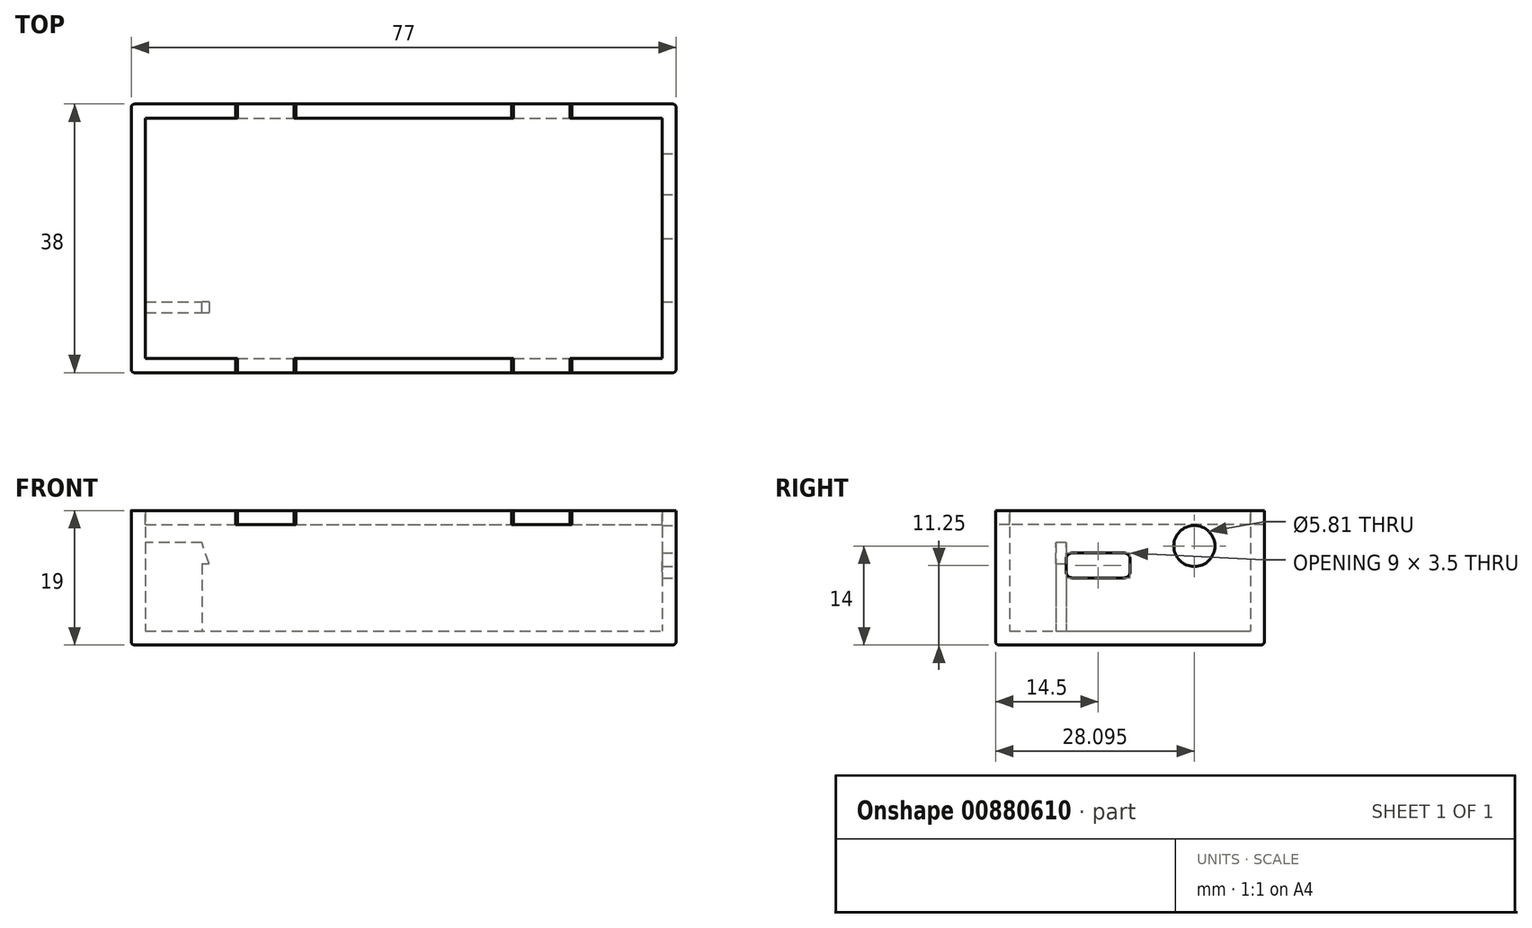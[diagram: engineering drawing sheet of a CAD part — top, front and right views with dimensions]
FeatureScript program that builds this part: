
annotation { "Feature Type Name" : "Feature", "Feature Type Description" : "" }
export const myFeature = defineFeature(function(context is Context, id is Id, definition is map)
    precondition{}
    {
        {
            var Q0;
            Q0=qCreatedBy(makeId("Top.planeOp"),FACE);
            var sketch = newSketch(context, id + "F0", { "sketchPlane" : qUnion([Q0])});
            skLineSegment(sketch, "E0.bottom", {"start": v(0, 0) * mm, "end": v(73, 0) * mm});
            skLineSegment(sketch, "E0.top", {"start": v(0, 34) * mm, "end": v(73, 34) * mm});
            skLineSegment(sketch, "E0.left", {"start": v(0, 0) * mm, "end": v(0, 34) * mm});
            skLineSegment(sketch, "E0.right", {"start": v(73, 0) * mm, "end": v(73, 34) * mm});
            skSolve(sketch);
        }
        {
            var Q0;
            Q0=makeQuery(id+"F0.imprint","IMPRINT",FACE,{"disambiguationData":[TD([[makeQuery(id+"F0.imprint","IMPRINT",EDGE,{"derivedFrom":sQuery(id+"F0.wireOp",EDGE,"E0.bottom")}),1.0]])]});
            extrude(context, id + "F1", {"entities" : qUnion([Q0]), "depth" : 17 * mm, "offsetDistance" : 25.4 * mm});
        }
        {
            var Q0;
            Q0=makeQuery(id+"F1.opExtrude","CAP_FACE",FACE,{"disambiguationData":[OSD([sQuery(id+"F0.wireOp",EDGE,"E0.bottom"),sQuery(id+"F0.wireOp",EDGE,"E0.top"),sQuery(id+"F0.wireOp",EDGE,"E0.left"),sQuery(id+"F0.wireOp",EDGE,"E0.right")])],"isStart":false});
            shell(context, id + "F2", {"entities" : qUnion([Q0]), "thickness" : 2 * mm, "oppositeDirection" : true});
        }
        {
            var Q0;
            Q0=makeQuery(id+"F1.opExtrude","SWEPT_FACE",FACE,{"disambiguationData":[OSD([sQuery(id+"F0.wireOp",EDGE,"E0.right")])]});
            var sketch = newSketch(context, id + "F3", { "sketchPlane" : qUnion([Q0])});
            skLineSegment(sketch, "E1.bottom", {"start": v(8, 11) * mm, "end": v(17, 11) * mm});
            skLineSegment(sketch, "E1.top", {"start": v(8, 7.5) * mm, "end": v(17, 7.5) * mm});
            skLineSegment(sketch, "E1.left", {"start": v(8, 11) * mm, "end": v(8, 7.5) * mm});
            skLineSegment(sketch, "E1.right", {"start": v(17, 11) * mm, "end": v(17, 7.5) * mm});
            skSolve(sketch);
        }
        {
            var Q0;
            Q0 = qSketchRegion(id + "F3", true);
            extrude(context, id + "F4", {"entities" : qUnion([Q0]), "operationType" : NewBodyOperationType.REMOVE, "oppositeDirection" : true, "depth" : 25.4 * mm, "offsetDistance" : 25.4 * mm});
        }
        {
            var Q0;
            Q0=makeQuery(id+"F1.opExtrude","SWEPT_FACE",FACE,{"disambiguationData":[OSD([sQuery(id+"F0.wireOp",EDGE,"E0.right")])]});
            var sketch = newSketch(context, id + "F5", { "sketchPlane" : qUnion([Q0])});
            skLineSegment(sketch, "E2", {"start": v(17.2, 12) * mm, "end": v(26.1, 12) * mm, "construction": true});
            skCircle(sketch, "E3", {"center": v(26.1, 12) * mm, "radius": 2.9 * mm});
            skSolve(sketch);
        }
        {
            var Q0;
            Q0 = qSketchRegion(id + "F5", true);
            extrude(context, id + "F6", {"entities" : qUnion([Q0]), "operationType" : NewBodyOperationType.REMOVE, "oppositeDirection" : true, "depth" : 25.4 * mm, "offsetDistance" : 25.4 * mm});
        }
        {
            var Q0;
            Q0=makeQuery(id+"F4.boolean.opBoolean","COPY",EDGE,{"derivedFrom":makeQuery(id+"F4.opExtrude","SWEPT_EDGE",EDGE,{"disambiguationData":[OSD([sQuery(id+"F3.wireOp",EDGE,"E1.top"),sQuery(id+"F3.wireOp",EDGE,"E1.left")])]})});
            var Q1;
            Q1=makeQuery(id+"F4.boolean.opBoolean","COPY",EDGE,{"derivedFrom":makeQuery(id+"F4.opExtrude","SWEPT_EDGE",EDGE,{"disambiguationData":[OSD([sQuery(id+"F3.wireOp",EDGE,"E1.bottom"),sQuery(id+"F3.wireOp",EDGE,"E1.right")])]})});
            var Q2;
            Q2=makeQuery(id+"F4.boolean.opBoolean","COPY",EDGE,{"derivedFrom":makeQuery(id+"F4.opExtrude","SWEPT_EDGE",EDGE,{"disambiguationData":[OSD([sQuery(id+"F3.wireOp",EDGE,"E1.top"),sQuery(id+"F3.wireOp",EDGE,"E1.right")])]})});
            var Q3;
            Q3=makeQuery(id+"F4.boolean.opBoolean","COPY",EDGE,{"derivedFrom":makeQuery(id+"F4.opExtrude","SWEPT_EDGE",EDGE,{"disambiguationData":[OSD([sQuery(id+"F3.wireOp",EDGE,"E1.bottom"),sQuery(id+"F3.wireOp",EDGE,"E1.left")])]})});
            fillet(context, id + "F7", {"entities" : qUnion([Q0, Q1, Q2, Q3]), "radius" : .8 * mm, "tangentPropagation" : true, "allowEdgeOverflow" : false});
        }
        {
            var Q0;
            Q0=makeQuery(id+"F1.opExtrude","SWEPT_EDGE",EDGE,{"disambiguationData":[OSD([sQuery(id+"F0.wireOp",EDGE,"E0.top"),sQuery(id+"F0.wireOp",EDGE,"E0.right")])]});
            var Q1;
            Q1=makeQuery(id+"F1.opExtrude","SWEPT_EDGE",EDGE,{"disambiguationData":[OSD([sQuery(id+"F0.wireOp",EDGE,"E0.top"),sQuery(id+"F0.wireOp",EDGE,"E0.left")])]});
            var Q2;
            Q2=makeQuery(id+"F1.opExtrude","SWEPT_EDGE",EDGE,{"disambiguationData":[OSD([sQuery(id+"F0.wireOp",EDGE,"E0.bottom"),sQuery(id+"F0.wireOp",EDGE,"E0.left")])]});
            var Q3;
            Q3=makeQuery(id+"F1.opExtrude","SWEPT_EDGE",EDGE,{"disambiguationData":[OSD([sQuery(id+"F0.wireOp",EDGE,"E0.bottom"),sQuery(id+"F0.wireOp",EDGE,"E0.right")])]});
            var Q4;
            Q4=makeQuery(id+"F1.opExtrude","CAP_EDGE",EDGE,{"disambiguationData":[OSD([sQuery(id+"F0.wireOp",EDGE,"E0.top")])],"isStart":true});
            var Q5;
            Q5=makeQuery(id+"F1.opExtrude","CAP_EDGE",EDGE,{"disambiguationData":[OSD([sQuery(id+"F0.wireOp",EDGE,"E0.right")])],"isStart":true});
            var Q6;
            Q6=makeQuery(id+"F1.opExtrude","CAP_EDGE",EDGE,{"disambiguationData":[OSD([sQuery(id+"F0.wireOp",EDGE,"E0.bottom")])],"isStart":true});
            var Q7;
            Q7=makeQuery(id+"F1.opExtrude","CAP_EDGE",EDGE,{"disambiguationData":[OSD([sQuery(id+"F0.wireOp",EDGE,"E0.left")])],"isStart":true});
            fillet(context, id + "F8", {"entities" : qUnion([Q0, Q1, Q2, Q3, Q4, Q5, Q6, Q7]), "radius" : .5 * mm, "tangentPropagation" : true, "allowEdgeOverflow" : false});
        }
        {
            var Q0;
            Q0=makeQuery(id+"F1.opExtrude","CAP_FACE",FACE,{"disambiguationData":[OSD([sQuery(id+"F0.wireOp",EDGE,"E0.bottom"),sQuery(id+"F0.wireOp",EDGE,"E0.top"),sQuery(id+"F0.wireOp",EDGE,"E0.left"),sQuery(id+"F0.wireOp",EDGE,"E0.right")])],"isStart":false});
            var sketch = newSketch(context, id + "F9", { "sketchPlane" : qUnion([Q0])});
            skLineSegment(sketch, "E4.bottom", {"start": v(60.25, 34) * mm, "end": v(51.75, 34) * mm});
            skLineSegment(sketch, "E4.top", {"start": v(60.25, 36) * mm, "end": v(51.75, 36) * mm});
            skLineSegment(sketch, "E4.left", {"start": v(60.25, 34) * mm, "end": v(60.25, 36) * mm});
            skLineSegment(sketch, "E4.right", {"start": v(51.75, 34) * mm, "end": v(51.75, 36) * mm});
            skLineSegment(sketch, "E5.bottom", {"start": v(21.25, 34) * mm, "end": v(12.75, 34) * mm});
            skLineSegment(sketch, "E5.top", {"start": v(21.25, 36) * mm, "end": v(12.75, 36) * mm});
            skLineSegment(sketch, "E5.left", {"start": v(21.25, 34) * mm, "end": v(21.25, 36) * mm});
            skLineSegment(sketch, "E5.right", {"start": v(12.75, 34) * mm, "end": v(12.75, 36) * mm});
            skLineSegment(sketch, "E6", {"start": v(0, 17) * mm, "end": v(73, 17) * mm, "construction": true});
            skLineSegment(sketch, "E7.MirrorCS", {"start": v(12.75, 0) * mm, "end": v(12.75, -2) * mm});
            skLineSegment(sketch, "E8.MirrorCS", {"start": v(21.25, -2) * mm, "end": v(12.75, -2) * mm});
            skLineSegment(sketch, "E9.MirrorCS", {"start": v(21.25, 0) * mm, "end": v(21.25, -2) * mm});
            skLineSegment(sketch, "E10.MirrorCS", {"start": v(21.25, 0) * mm, "end": v(12.75, 0) * mm});
            skLineSegment(sketch, "E11.MirrorCS", {"start": v(60.25, -2) * mm, "end": v(51.75, -2) * mm});
            skLineSegment(sketch, "E12.MirrorCS", {"start": v(60.25, 0) * mm, "end": v(60.25, -2) * mm});
            skLineSegment(sketch, "E13.MirrorCS", {"start": v(60.25, 0) * mm, "end": v(51.75, 0) * mm});
            skLineSegment(sketch, "E14.MirrorCS", {"start": v(51.75, 0) * mm, "end": v(51.75, -2) * mm});
            skLineSegment(sketch, "E15", {"start": v(17, 36) * mm, "end": v(17, 39.81) * mm, "construction": true});
            skLineSegment(sketch, "E16", {"start": v(56, 36) * mm, "end": v(56, 40) * mm, "construction": true});
            skSolve(sketch);
        }
        {
            var Q0;
            Q0=makeQuery(id+"F9.imprint","IMPRINT",FACE,{"disambiguationData":[TD([[makeQuery(id+"F9.imprint","IMPRINT",EDGE,{"derivedFrom":sQuery(id+"F9.wireOp",EDGE,"E5.bottom")}),1.0]])]});
            var Q1;
            Q1=makeQuery(id+"F9.imprint","IMPRINT",FACE,{"disambiguationData":[TD([[makeQuery(id+"F9.imprint","IMPRINT",EDGE,{"derivedFrom":sQuery(id+"F9.wireOp",EDGE,"E4.bottom")}),1.0]])]});
            var Q2;
            Q2=makeQuery(id+"F9.imprint","IMPRINT",FACE,{"disambiguationData":[TD([[makeQuery(id+"F9.imprint","IMPRINT",EDGE,{"derivedFrom":sQuery(id+"F9.wireOp",EDGE,"E11.MirrorCS")}),1.0]])]});
            var Q3;
            Q3=makeQuery(id+"F9.imprint","IMPRINT",FACE,{"disambiguationData":[TD([[makeQuery(id+"F9.imprint","IMPRINT",EDGE,{"derivedFrom":sQuery(id+"F9.wireOp",EDGE,"E7.MirrorCS")}),1.0]])]});
            extrude(context, id + "F10", {"entities" : qUnion([Q0, Q1, Q2, Q3]), "operationType" : NewBodyOperationType.REMOVE, "oppositeDirection" : true, "depth" : 2 * mm, "offsetDistance" : 25.4 * mm});
        }
        {
            var Q0;
            {var subQ0=sQuery(id+"F0.wireOp",EDGE,"E0.bottom");var subQ1=sQuery(id+"F0.wireOp",EDGE,"E0.left");var subQ2=sQuery(id+"F0.wireOp",EDGE,"E0.top");Q0=makeQuery(id+"F10.boolean.opBoolean","SPLIT",FACE,{"disambiguationData":[TD([makeQuery(id+"F1.opExtrude","SWEPT_FACE",FACE,{"disambiguationData":[OSD([subQ1])]})])],"derivedFrom":makeQuery(id+"F1.opExtrude","CAP_FACE",FACE,{"disambiguationData":[OSD([subQ0,subQ2,subQ1,sQuery(id+"F0.wireOp",EDGE,"E0.right")])],"isStart":false})});}
            var sketch = newSketch(context, id + "F11", { "sketchPlane" : qUnion([Q0])});
            skLineSegment(sketch, "E17.top", {"start": v(0, 0) * mm, "end": v(13, 0) * mm});
            skLineSegment(sketch, "E17.left", {"start": v(0, 34) * mm, "end": v(0, 0) * mm});
            skLineSegment(sketch, "E17.right", {"start": v(73, 34) * mm, "end": v(73, 0) * mm});
            skLineSegment(sketch, "E18", {"start": v(0, 17) * mm, "end": v(73, 17) * mm, "construction": true});
            skLineSegment(sketch, "E19", {"start": v(13, 0) * mm, "end": v(13, -2) * mm});
            skLineSegment(sketch, "E20", {"start": v(13, -2) * mm, "end": v(21, -2) * mm});
            skLineSegment(sketch, "E21", {"start": v(21, -2) * mm, "end": v(21, 0) * mm});
            skLineSegment(sketch, "E22", {"start": v(21, 0) * mm, "end": v(52, 0) * mm});
            skLineSegment(sketch, "E23", {"start": v(52, 0) * mm, "end": v(52, -2) * mm});
            skLineSegment(sketch, "E24", {"start": v(52, -2) * mm, "end": v(60, -2) * mm});
            skLineSegment(sketch, "E25", {"start": v(60, -2) * mm, "end": v(60, 0) * mm});
            skLineSegment(sketch, "E26", {"start": v(60, 0) * mm, "end": v(73, 0) * mm});
            skLineSegment(sketch, "E27.MirrorCS", {"start": v(0, 34) * mm, "end": v(13, 34) * mm});
            skLineSegment(sketch, "E28.MirrorCS", {"start": v(13, 34) * mm, "end": v(13, 36) * mm});
            skLineSegment(sketch, "E29.MirrorCS", {"start": v(13, 36) * mm, "end": v(21, 36) * mm});
            skLineSegment(sketch, "E30.MirrorCS", {"start": v(21, 36) * mm, "end": v(21, 34) * mm});
            skLineSegment(sketch, "E31.MirrorCS", {"start": v(21, 34) * mm, "end": v(52, 34) * mm});
            skLineSegment(sketch, "E32.MirrorCS", {"start": v(52, 34) * mm, "end": v(52, 36) * mm});
            skLineSegment(sketch, "E33.MirrorCS", {"start": v(52, 36) * mm, "end": v(60, 36) * mm});
            skLineSegment(sketch, "E34.MirrorCS", {"start": v(60, 36) * mm, "end": v(60, 34) * mm});
            skLineSegment(sketch, "E35.MirrorCS", {"start": v(60, 34) * mm, "end": v(73, 34) * mm});
            skSolve(sketch);
        }
        {
            var Q0;
            Q0 = qSketchRegion(id + "F11", true);
            extrude(context, id + "F12", {"entities" : qUnion([Q0]), "oppositeDirection" : true, "depth" : 2 * mm, "offsetDistance" : 25.4 * mm});
        }
        {
            var Q0;
            Q0=makeQuery(id+"F2.opShell","OFFSET_FACE",FACE,{"disambiguationData":[OSD([sQuery(id+"F0.wireOp",EDGE,"E0.bottom"),sQuery(id+"F0.wireOp",EDGE,"E0.top"),sQuery(id+"F0.wireOp",EDGE,"E0.left"),sQuery(id+"F0.wireOp",EDGE,"E0.right")])]});
            var sketch = newSketch(context, id + "F13", { "sketchPlane" : qUnion([Q0])});
            skLineSegment(sketch, "E36.bottom", {"start": v(0, 8) * mm, "end": v(8, 8) * mm});
            skLineSegment(sketch, "E36.top", {"start": v(0, 6.5) * mm, "end": v(8, 6.5) * mm});
            skLineSegment(sketch, "E36.left", {"start": v(0, 6.5) * mm, "end": v(0, 8) * mm});
            skLineSegment(sketch, "E36.right", {"start": v(8, 6.5) * mm, "end": v(8, 8) * mm});
            skSolve(sketch);
        }
        {
            var Q0;
            Q0 = qSketchRegion(id + "F13", true);
            extrude(context, id + "F14", {"entities" : qUnion([Q0]), "operationType" : NewBodyOperationType.ADD, "depth" : 9.5 * mm, "offsetDistance" : 25.4 * mm});
        }
        {
            var Q0;
            Q0=makeQuery(id+"F14.opExtrude","SWEPT_FACE",FACE,{"disambiguationData":[OSD([sQuery(id+"F13.wireOp",EDGE,"E36.top")])]});
            var sketch = newSketch(context, id + "F15", { "sketchPlane" : qUnion([Q0])});
            skLineSegment(sketch, "E37", {"start": v(0, 9.5) * mm, "end": v(9, 9.5) * mm});
            skLineSegment(sketch, "E38", {"start": v(9, 9.5) * mm, "end": v(8, 12.5) * mm});
            skLineSegment(sketch, "E39", {"start": v(8, 12.5) * mm, "end": v(0, 12.5) * mm});
            skLineSegment(sketch, "E40", {"start": v(0, 12.5) * mm, "end": v(0, 9.5) * mm});
            skSolve(sketch);
        }
        {
            var Q0;
            Q0 = qSketchRegion(id + "F15", true);
            extrude(context, id + "F16", {"entities" : qUnion([Q0]), "operationType" : NewBodyOperationType.ADD, "oppositeDirection" : true, "depth" : 1.5 * mm, "offsetDistance" : 25.4 * mm});
        }
    });
